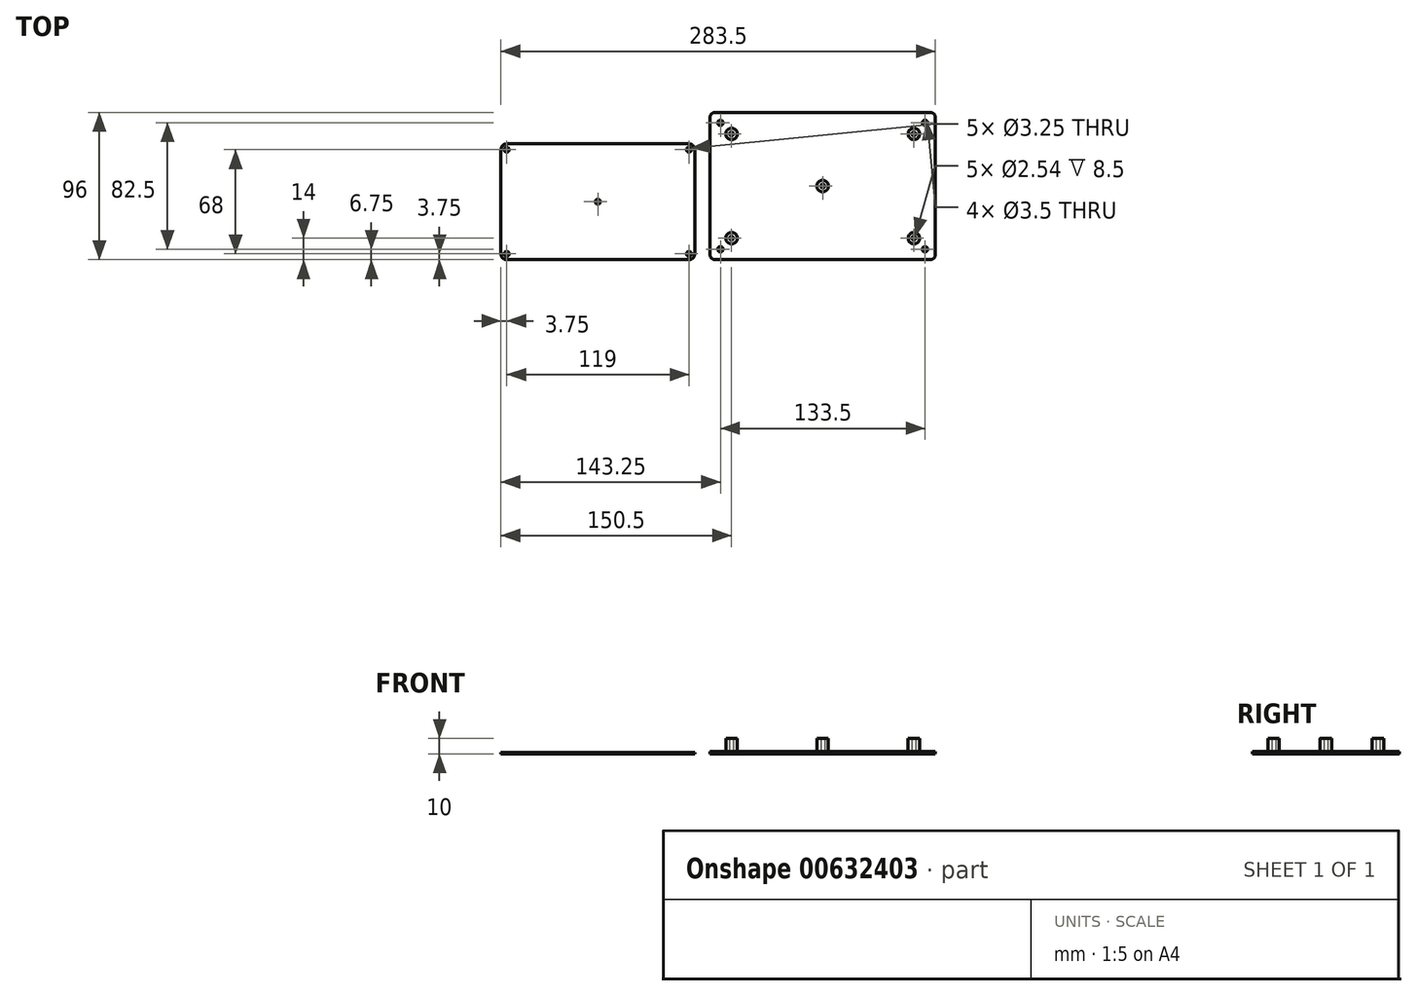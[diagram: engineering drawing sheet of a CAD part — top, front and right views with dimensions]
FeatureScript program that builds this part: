
annotation { "Feature Type Name" : "Feature", "Feature Type Description" : "" }
export const myFeature = defineFeature(function(context is Context, id is Id, definition is map)
    precondition{}
    {
        {
            var Q0;
            Q0=qCreatedBy(makeId("Top.planeOp"),FACE);
            var sketch = newSketch(context, id + "F0", { "sketchPlane" : qUnion([Q0])});
            skLineSegment(sketch, "E0.bottom", {"start": v(8.2, 5) * mm, "end": v(148.8, 5) * mm});
            skLineSegment(sketch, "E0.top", {"start": v(8.2, 101) * mm, "end": v(148.8, 101) * mm});
            skLineSegment(sketch, "E0.left", {"start": v(5, 8.2) * mm, "end": v(5, 97.8) * mm});
            skLineSegment(sketch, "E0.right", {"start": v(152, 8.2) * mm, "end": v(152, 97.8) * mm});
            skPoint(sketch, "E1.visualSharp", {"position": v(5, 101) * mm});
            skArc(sketch, "E1.filletArc", {"start": v(8.2, 101) * mm, "mid": v(5.94, 100.06) * mm, "end": v(5, 97.8) * mm});
            skPoint(sketch, "E2.visualSharp", {"position": v(5, 5) * mm});
            skArc(sketch, "E2.filletArc", {"start": v(5, 8.2) * mm, "mid": v(5.94, 5.94) * mm, "end": v(8.2, 5) * mm});
            skPoint(sketch, "E3.visualSharp", {"position": v(152, 5) * mm});
            skArc(sketch, "E3.filletArc", {"start": v(148.8, 5) * mm, "mid": v(151.06, 5.94) * mm, "end": v(152, 8.2) * mm});
            skPoint(sketch, "E4.visualSharp", {"position": v(152, 101) * mm});
            skArc(sketch, "E4.filletArc", {"start": v(152, 97.8) * mm, "mid": v(151.06, 100.06) * mm, "end": v(148.8, 101) * mm});
            skCircle(sketch, "E5", {"center": v(145.25, 11.75) * mm, "radius": 1.75 * mm});
            skCircle(sketch, "E6", {"center": v(145.25, 94.25) * mm, "radius": 1.75 * mm});
            skCircle(sketch, "E7", {"center": v(11.75, 94.25) * mm, "radius": 1.75 * mm});
            skCircle(sketch, "E8", {"center": v(11.75, 11.75) * mm, "radius": 1.75 * mm});
            skSolve(sketch);
        }
        {
            var Q0;
            Q0 = qSketchRegion(id + "F0", true);
            extrude(context, id + "F1", {"entities" : qUnion([Q0]), "depth" : 1.5 * mm, "offsetDistance" : 25 * mm});
        }
        {
            var Q0;
            Q0=makeQuery(id+"F1.opExtrude","CAP_FACE",FACE,{"disambiguationData":[OSD([sQuery(id+"F0.wireOp",EDGE,"E0.bottom"),sQuery(id+"F0.wireOp",EDGE,"E0.top"),sQuery(id+"F0.wireOp",EDGE,"E0.left"),sQuery(id+"F0.wireOp",EDGE,"E0.right"),sQuery(id+"F0.wireOp",EDGE,"E1.filletArc"),sQuery(id+"F0.wireOp",EDGE,"E2.filletArc"),sQuery(id+"F0.wireOp",EDGE,"E3.filletArc"),sQuery(id+"F0.wireOp",EDGE,"E4.filletArc"),sQuery(id+"F0.wireOp",EDGE,"E5"),sQuery(id+"F0.wireOp",EDGE,"E6"),sQuery(id+"F0.wireOp",EDGE,"E7"),sQuery(id+"F0.wireOp",EDGE,"E8")])],"isStart":false});
            var sketch = newSketch(context, id + "F2", { "sketchPlane" : qUnion([Q0])});
            skCircle(sketch, "E9", {"center": v(19, 19) * mm, "radius": 3.75 * mm});
            skCircle(sketch, "E10", {"center": v(138, 19) * mm, "radius": 3.75 * mm});
            skCircle(sketch, "E11", {"center": v(138, 87) * mm, "radius": 3.75 * mm});
            skCircle(sketch, "E12", {"center": v(19, 87) * mm, "radius": 3.75 * mm});
            skCircle(sketch, "E13", {"center": v(19, 87) * mm, "radius": 1.27 * mm});
            skCircle(sketch, "E14", {"center": v(19, 19) * mm, "radius": 1.27 * mm});
            skCircle(sketch, "E15", {"center": v(138, 19) * mm, "radius": 1.27 * mm});
            skCircle(sketch, "E16", {"center": v(138, 87) * mm, "radius": 1.27 * mm});
            skCircle(sketch, "E17", {"center": v(78.5, 53) * mm, "radius": 3.75 * mm});
            skCircle(sketch, "E18", {"center": v(78.5, 53) * mm, "radius": 1.27 * mm});
            skPoint(sketch, "E19", {"position": v(152, 53) * mm});
            skPoint(sketch, "E20", {"position": v(78.5, 5) * mm});
            skSolve(sketch);
        }
        {
            var Q0;
            Q0 = qSketchRegion(id + "F2", true);
            extrude(context, id + "F3", {"entities" : qUnion([Q0]), "operationType" : NewBodyOperationType.ADD, "depth" : 8.5 * mm, "offsetDistance" : 25 * mm});
        }
        {
            var Q0;
            Q0=qCreatedBy(makeId("Top.planeOp"),FACE);
            var sketch = newSketch(context, id + "F4", { "sketchPlane" : qUnion([Q0])});
            skLineSegment(sketch, "E21.bottom", {"start": v(-8.75, 5) * mm, "end": v(-127.75, 5) * mm});
            skLineSegment(sketch, "E21.top", {"start": v(-8.75, 80.5) * mm, "end": v(-127.75, 80.5) * mm});
            skLineSegment(sketch, "E21.left", {"start": v(-5, 8.75) * mm, "end": v(-5, 76.75) * mm});
            skLineSegment(sketch, "E21.right", {"start": v(-131.5, 8.75) * mm, "end": v(-131.5, 76.75) * mm});
            skPoint(sketch, "E22.visualSharp", {"position": v(-5, 5) * mm});
            skArc(sketch, "E22.filletArc", {"start": v(-8.75, 5) * mm, "mid": v(-6.1, 6.1) * mm, "end": v(-5, 8.75) * mm});
            skPoint(sketch, "E23.visualSharp", {"position": v(-5, 80.5) * mm});
            skArc(sketch, "E23.filletArc", {"start": v(-5, 76.75) * mm, "mid": v(-6.1, 79.4) * mm, "end": v(-8.75, 80.5) * mm});
            skPoint(sketch, "E24.visualSharp", {"position": v(-131.5, 80.5) * mm});
            skArc(sketch, "E24.filletArc", {"start": v(-127.75, 80.5) * mm, "mid": v(-130.4, 79.4) * mm, "end": v(-131.5, 76.75) * mm});
            skPoint(sketch, "E25.visualSharp", {"position": v(-131.5, 5) * mm});
            skArc(sketch, "E25.filletArc", {"start": v(-131.5, 8.75) * mm, "mid": v(-130.4, 6.1) * mm, "end": v(-127.75, 5) * mm});
            skCircle(sketch, "E26", {"center": v(-8.75, 8.75) * mm, "radius": 1.63 * mm});
            skCircle(sketch, "E27", {"center": v(-8.75, 76.75) * mm, "radius": 1.63 * mm});
            skCircle(sketch, "E28", {"center": v(-127.75, 76.75) * mm, "radius": 1.63 * mm});
            skCircle(sketch, "E29", {"center": v(-127.75, 8.75) * mm, "radius": 1.63 * mm});
            skCircle(sketch, "E30", {"center": v(-68.25, 42.75) * mm, "radius": 1.63 * mm});
            skPoint(sketch, "E31", {"position": v(-68.25, 80.5) * mm});
            skPoint(sketch, "E32", {"position": v(-5, 42.75) * mm});
            skSolve(sketch);
        }
        {
            var Q0;
            Q0 = qSketchRegion(id + "F4", true);
            extrude(context, id + "F5", {"entities" : qUnion([Q0]), "depth" : 1 * mm, "offsetDistance" : 25 * mm});
        }
    });
